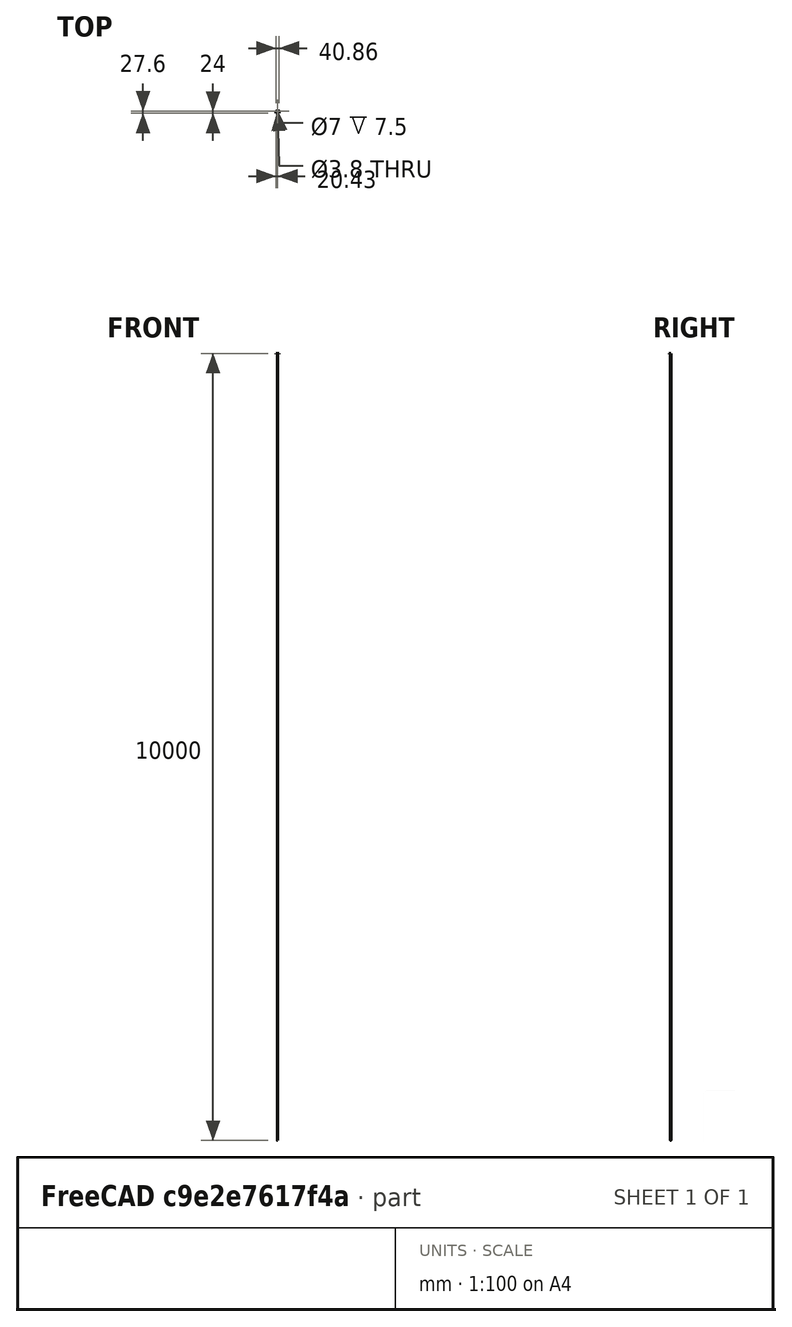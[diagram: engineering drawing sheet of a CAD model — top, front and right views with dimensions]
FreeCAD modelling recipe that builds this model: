
FCSTD DOCUMENT  (FreeCAD 0.16R)
Label: BoatLatch2
License: All rights reserved
LicenseURL: http://en.wikipedia.org/wiki/All_rights_reserved
objects: Sketcher::SketchObject×5, PartDesign::Pocket×4, PartDesign::Fillet×2, PartDesign::Pad×1, PartDesign::Chamfer×1, Mesh::Feature×1
note: 18 computed .brp shape members not serialized (recipe doc carries the construction recipe); baked Part::Feature solids carry a one-line shape summary decoded from their .brp

FEATURE [Sketcher::SketchObject] Sketch
  sketch-geometry (4):
    g0: LineSegment StartX=-19 StartY=9 StartZ=0 EndX=19 EndY=9 EndZ=0
    g1: LineSegment StartX=19 StartY=9 StartZ=0 EndX=19 EndY=-8 EndZ=0
    g2: LineSegment StartX=19 StartY=-8 StartZ=0 EndX=-19 EndY=-8 EndZ=0
    g3: LineSegment StartX=-19 StartY=-8 StartZ=0 EndX=-19 EndY=9 EndZ=0
  constraints (11):
    c: Coincident(g0,g1)
    c: Coincident(g1,g2)
    c: Coincident(g2,g3)
    c: Coincident(g3,g0)
    c: Horizontal(g0)
    c: Horizontal(g2)
    c: Vertical(g1)
    c: Vertical(g3)
    c: DistanceX(g0,g0) = 38
    c: DistanceY(g3,g3) = 17
    c: DistanceY(g0) = 9
FEATURE [PartDesign::Pad] Pad
  Length = 9.5
  Length2 = 100
  Sketch = -> Sketch
  Type = 0
FEATURE [Sketcher::SketchObject] Sketch001
  Placement = pos=(0,0,9.5) rot=(0,0,1;0rad)
  Support = -> Pad [Face6]
  sketch-geometry (1):
    g0: Circle CenterX=0 CenterY=5.4 CenterZ=0 NormalX=0 NormalY=0 NormalZ=1 Radius=1.9
  constraints (3):
    c: Radius(g0) = 1.9
    c: PointOnObject(g0,g-2)
    c: DistanceY(g-1,g0) = 5.4
FEATURE [PartDesign::Pocket] Pocket
  Length = 5
  Sketch = -> Sketch001
  Type = 1
FEATURE [Sketcher::SketchObject] Sketch002
  ExternalGeometry = -> [Pocket]
  Placement = pos=(0,0,9.5) rot=(0,0,1;0rad)
  Support = -> Pocket [Face5]
  sketch-geometry (4):
    g0: LineSegment StartX=-20.4338 StartY=-18.6 StartZ=0 EndX=20.4338 EndY=-18.6 EndZ=0
    g1: LineSegment StartX=20.4338 StartY=-18.6 StartZ=0 EndX=20.4338 EndY=1.4 EndZ=0
    g2: LineSegment StartX=20.4338 StartY=1.4 StartZ=0 EndX=-20.4338 EndY=1.4 EndZ=0
    g3: LineSegment StartX=-20.4338 StartY=1.4 StartZ=0 EndX=-20.4338 EndY=-18.6 EndZ=0
  constraints (12):
    c: Coincident(g0,g1)
    c: Coincident(g1,g2)
    c: Coincident(g2,g3)
    c: Coincident(g3,g0)
    c: Horizontal(g0)
    c: Horizontal(g2)
    c: Vertical(g1)
    c: Vertical(g3)
    c: DistanceX(g0,g0) = 40.8677
    c: DistanceY(g3,g3) = -20
    c: Symmetric(g1,g2,g-2)
    c: Distance(g-3,g2) = 4
FEATURE [PartDesign::Pocket] Pocket001
  Length = 5.5
  Sketch = -> Sketch002
  Type = 0
FEATURE [Sketcher::SketchObject] Sketch003
  ExternalGeometry = -> [Pocket001]
  Placement = pos=(0,0,9.5) rot=(0,0,1;0rad)
  Support = -> Pocket001 [Face5]
  sketch-geometry (1):
    g0: Circle CenterX=0 CenterY=5.4 CenterZ=0 NormalX=0 NormalY=0 NormalZ=1 Radius=3.5
  constraints (2):
    c: Radius(g0) = 3.5
    c: Coincident(g0,g-3)
FEATURE [PartDesign::Pocket] Pocket002
  Length = 7.5
  Sketch = -> Sketch003
  Type = 0
FEATURE [Sketcher::SketchObject] Sketch004
  Placement = pos=(-19,0,0) rot=(0.57735,-0.57735,-0.57735;2.0944rad)
  Support = -> Pocket002 [Face2]
  sketch-geometry (3):
    g0: LineSegment StartX=-11.5 StartY=11 StartZ=0 EndX=0 EndY=7 EndZ=0
    g1: LineSegment StartX=0 StartY=7 StartZ=0 EndX=0 EndY=11 EndZ=0
    g2: LineSegment StartX=0 StartY=11 StartZ=0 EndX=-11.5 EndY=11 EndZ=0
  constraints (9):
    c: Coincident(g0,g1)
    c: Coincident(g1,g2)
    c: Horizontal(g2)
    c: Coincident(g0,g2)
    c: PointOnObject(g0,g-2)
    c: PointOnObject(g1,g-2)
    c: DistanceY(g0) = 7
    c: DistanceY(g1) = 11
    c: DistanceX(g0) = -11.5
FEATURE [PartDesign::Pocket] Pocket003
  Length = 5
  Sketch = -> Sketch004
  Type = 1
FEATURE [PartDesign::Fillet] Fillet
  Base = -> Pocket003 [Edge12,Edge10]
  Radius = 3
FEATURE [PartDesign::Chamfer] Chamfer
  Base = -> Fillet [Edge11,Edge10,Edge1]
  Size = 3
FEATURE [PartDesign::Fillet] Fillet001
  Base = -> Chamfer [Edge19,Edge12,Edge36,Edge35,Edge21,Edge20,Edge39,Edge13,Edge2,Edge4,Edge34,Edge40,Edge8]
  Radius = 1
FEATURE [Mesh::Feature] Mesh  label="Fillet001 (Meshed)"
